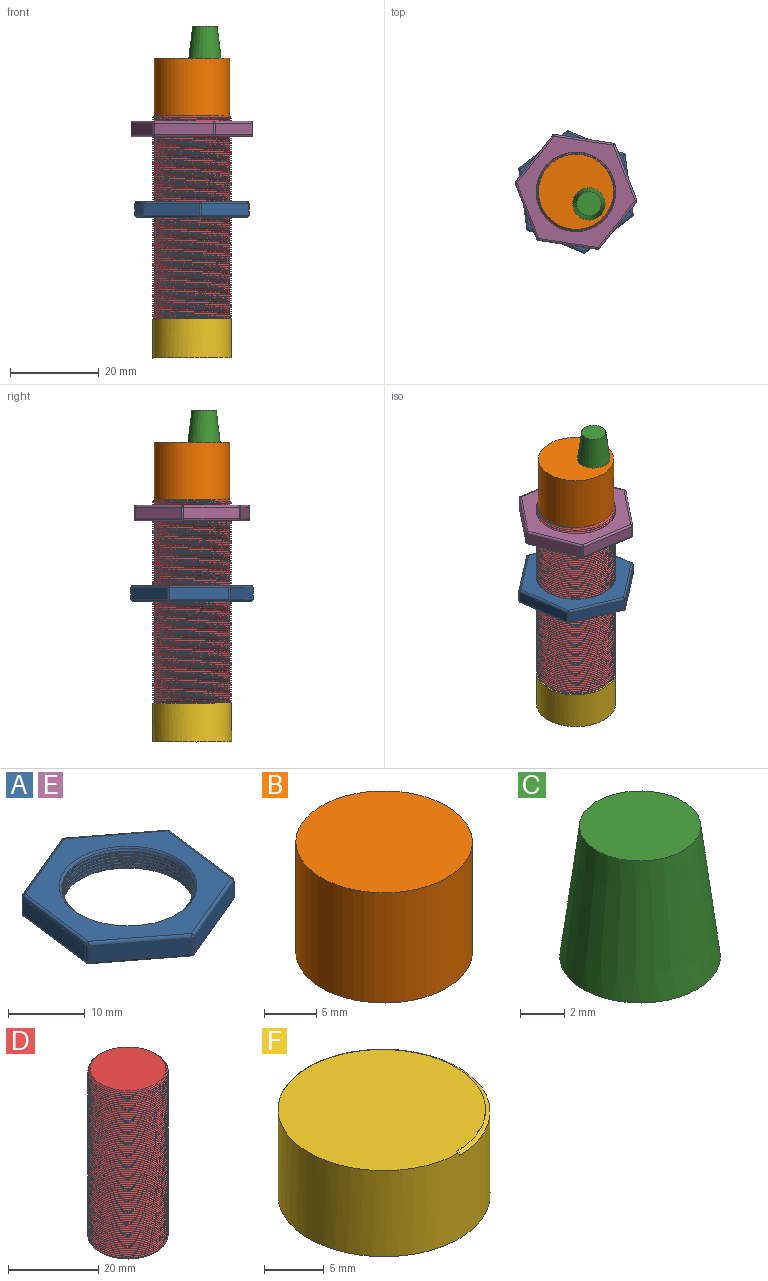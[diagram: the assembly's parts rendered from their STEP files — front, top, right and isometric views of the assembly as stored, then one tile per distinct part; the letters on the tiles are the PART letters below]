
ASSEMBLY  parts=6 mates=5
PART A: 44 faces, bbox 25.7x27.6x3.7 mm
  f0: cone r=8.97mm half-angle=45deg, axis (0,0,-1), area 28.1mm2, adj f7,f10,f41,f42,f43
  f1: cone r=8.47mm half-angle=45deg, axis (0,0,1), area 28.2mm2, adj f7,f9,f41,f42,f43
  f2: plane 10.69x8.17mm, normal (0.61,0.79,0), area 34.8mm2, adj f29,f34,f37,f40
  f3: plane 12.42x5.18mm, normal (-0.38,0.92,0), area 34.8mm2, adj f26,f35,f36,f40
  f4: plane 13.34x2.59mm, normal (-0.99,0.13,0), area 34.8mm2, adj f16,f25,f26,f27
  f5: plane 10.69x8.17mm, normal (-0.61,-0.79,0), area 34.8mm2, adj f11,f15,f16,f17
  f6: plane 12.42x5.18mm, normal (0.38,-0.92,0), area 34.8mm2, adj f11,f14,f18,f19
  f7: cylinder r=8.47mm len=16.95mm, axis (0,0,-1), area 66.1mm2, adj f0,f1,f42,f43
  f8: plane 13.34x2.59mm, normal (0.99,-0.13,0), area 34.8mm2, adj f19,f24,f28,f29
  f9: plane 26.69x24.84mm, normal (0,0,1), area 217.3mm2, adj f1,f14,f15,f24,f25,f34,f35
  f10: plane 26.69x24.84mm, normal (0,0,-1), area 217.3mm2, adj f0,f17,f18,f27,f28,f36,f37
  f11: cylinder r=0.45mm len=2.59mm, axis (0,0,-1), area 1.2mm2, adj f5,f6,f12,f13
  f12: sphere r=0.45mm, area 0.2mm2, adj f11,f14,f15
  f13: sphere r=0.45mm, area 0.1mm2, adj f11,f17,f18
  f14: cylinder r=0.45mm len=12.59mm, axis (-0.92,-0.38,0), area 9.4mm2, adj f6,f9,f12,f20
  f15: cylinder r=0.45mm len=10.96mm, axis (-0.79,0.61,0), area 9.4mm2, adj f5,f9,f12,f21
  f16: cylinder r=0.45mm len=2.59mm, axis (0,0,-1), area 1.2mm2, adj f4,f5,f21,f22
  f17: cylinder r=0.45mm len=10.96mm, axis (0.79,-0.61,0), area 9.4mm2, adj f5,f10,f13,f22
  f18: cylinder r=0.45mm len=12.59mm, axis (0.92,0.38,0), area 9.4mm2, adj f6,f10,f13,f23
  f19: cylinder r=0.45mm len=2.59mm, axis (0,0,-1), area 1.2mm2, adj f6,f8,f20,f23
  f20: sphere r=0.45mm, area 0.2mm2, adj f14,f19,f24
  f21: sphere r=0.45mm, area 0.2mm2, adj f15,f16,f25
  f22: sphere r=0.45mm, area 0.2mm2, adj f16,f17,f27
  f23: sphere r=0.45mm, area 0.2mm2, adj f18,f19,f28
  f24: cylinder r=0.45mm len=13.4mm, axis (-0.13,-0.99,0), area 9.4mm2, adj f8,f9,f20,f30
  f25: cylinder r=0.45mm len=13.4mm, axis (0.13,0.99,0), area 9.4mm2, adj f4,f9,f21,f31
  f26: cylinder r=0.45mm len=2.59mm, axis (0,0,-1), area 1.2mm2, adj f3,f4,f31,f32
  f27: cylinder r=0.45mm len=13.4mm, axis (-0.13,-0.99,0), area 9.4mm2, adj f4,f10,f22,f32
  f28: cylinder r=0.45mm len=13.4mm, axis (0.13,0.99,0), area 9.4mm2, adj f8,f10,f23,f33
  f29: cylinder r=0.45mm len=2.59mm, axis (0,0,-1), area 1.2mm2, adj f2,f8,f30,f33
  f30: sphere r=0.45mm, area 0.2mm2, adj f24,f29,f34
  f31: sphere r=0.45mm, area 0.2mm2, adj f25,f26,f35
  f32: sphere r=0.45mm, area 0.2mm2, adj f26,f27,f36
  f33: sphere r=0.45mm, area 0.1mm2, adj f28,f29,f37
  f34: cylinder r=0.45mm len=10.96mm, axis (0.79,-0.61,0), area 9.4mm2, adj f2,f9,f30,f38
  f35: cylinder r=0.45mm len=12.59mm, axis (0.92,0.38,0), area 9.4mm2, adj f3,f9,f31,f38
  f36: cylinder r=0.45mm len=12.59mm, axis (-0.92,-0.38,0), area 9.4mm2, adj f3,f10,f32,f39
  f37: cylinder r=0.45mm len=10.96mm, axis (-0.79,0.61,0), area 9.4mm2, adj f2,f10,f33,f39
  f38: sphere r=0.45mm, area 0.4mm2, adj f34,f35,f40
  f39: sphere r=0.45mm, area 0.3mm2, adj f36,f37,f40
  f40: cylinder r=0.45mm len=2.59mm, axis (0,0,-1), area 1.2mm2, adj f2,f3,f38,f39
  f41: bspline ~20.28x17.56mm, area 140.5mm2, adj f0,f1,f42,f43
  f42: bspline ~19.76x17.11mm, area 44.2mm2, adj f0,f1,f7,f41
  f43: bspline ~20.28x17.56mm, area 92.2mm2, adj f0,f1,f7,f41
PART B: 3 faces, bbox 17x17x13 mm
  f0: cylinder r=8.47mm len=16.95mm, axis (0,0,-1), area 689.6mm2, adj f1,f2
  f1: plane 16.95x16.95mm, normal (0,0,1), area 225.6mm2, adj f0
  f2: plane 16.95x16.95mm, normal (0,0,-1), area 225.6mm2, adj f0
PART C: 3 faces, bbox 7.3x7.3x7.3 mm
  f0: cone r=3.65mm half-angle=7deg, axis (0,0,-1), area 147mm2, adj f1,f2
  f1: plane 5.51x5.51mm, normal (0,0,1), area 23.8mm2, adj f0
  f2: plane 7.29x7.29mm, normal (0,0,-1), area 41.7mm2, adj f0
PART D: 8 faces, bbox 20.6x17.8x46 mm
  f0: cone r=8.41mm half-angle=45deg, axis (0,0,-1), area 24.3mm2, adj f1,f4,f6,f7
  f1: cone r=8.41mm half-angle=45deg, axis (0,0,-1), area 0.5mm2, adj f0,f3,f7
  f2: cone r=8.91mm half-angle=45deg, axis (0,0,1), area 24.8mm2, adj f3,f5,f6,f7
  f3: cylinder r=8.91mm len=44.78mm, axis (0,0,-1), area 68.7mm2, adj f1,f2,f6,f7
  f4: plane 16.82x16.82mm, normal (0,0,1), area 222.2mm2, adj f0
  f5: plane 16.82x16.82mm, normal (0,0,-1), area 222.2mm2, adj f2
  f6: bspline ~45.81x20.58mm, area 2210.6mm2, adj f0,f2,f3,f7
  f7: bspline ~45.81x20.58mm, area 2224.2mm2, adj f0,f1,f2,f3,f6
PART E: same geometry as A
PART F: 6 faces, bbox 19.6x18.2x9.5 mm
  f0: cylinder r=8.91mm len=17.82mm, axis (0,0,1), area 490.6mm2, adj f1,f2,f3,f5
  f1: plane 18.14x17.92mm, normal (0,0,1), area 242mm2, adj f0,f3,f4,f5
  f2: plane 17.82x17.82mm, normal (0,0,-1), area 249.4mm2, adj f0
  f3: plane 0.39x0.3mm, normal (1,0,0), area 0.1mm2, adj f0,f1,f4,f5
  f4: bspline ~7.72x4.65mm, area 0.5mm2, adj f1,f3,f5
  f5: bspline ~18x17.82mm, area 9mm2, adj f0,f1,f3,f4
PLACE A rot(axis=(0,0,-1),105deg) t=(-30.18,-8.31,10.89)mm
PLACE B rot(axis=(0,0,1),137deg) t=(-30.18,-8.31,-12)mm
PLACE C rot(axis=(0,0,1),137deg) t=(-30.4,-14.41,-12)mm
PLACE D rot(axis=(0,0,1),137deg) t=(-30.18,-8.31,-12)mm
PLACE E rot(axis=(0,0,1),28.8deg) t=(-30.18,-8.31,29.03)mm
PLACE F rot(axis=(0,0,1),137deg) t=(-30.18,-8.31,-12)mm
MATE cylindrical E.f0 <-> B.f0  axis (0,0,-1) through (-30.18,-8.31,29.03)mm
MATE fastened D.f0 <-> F.f0  axis (0,0,-1) through (-30.18,-8.31,-12)mm
MATE cylindrical A.f0 <-> B.f0  axis (0,0,-1) through (-30.18,-8.31,10.89)mm
MATE fastened C.f0 <-> B.f1  axis (0,0,-1) through (-27.25,-11.04,46.73)mm
MATE fastened B.f0 <-> D.f0  axis (0,0,-1) through (-30.18,-8.31,33.78)mm
